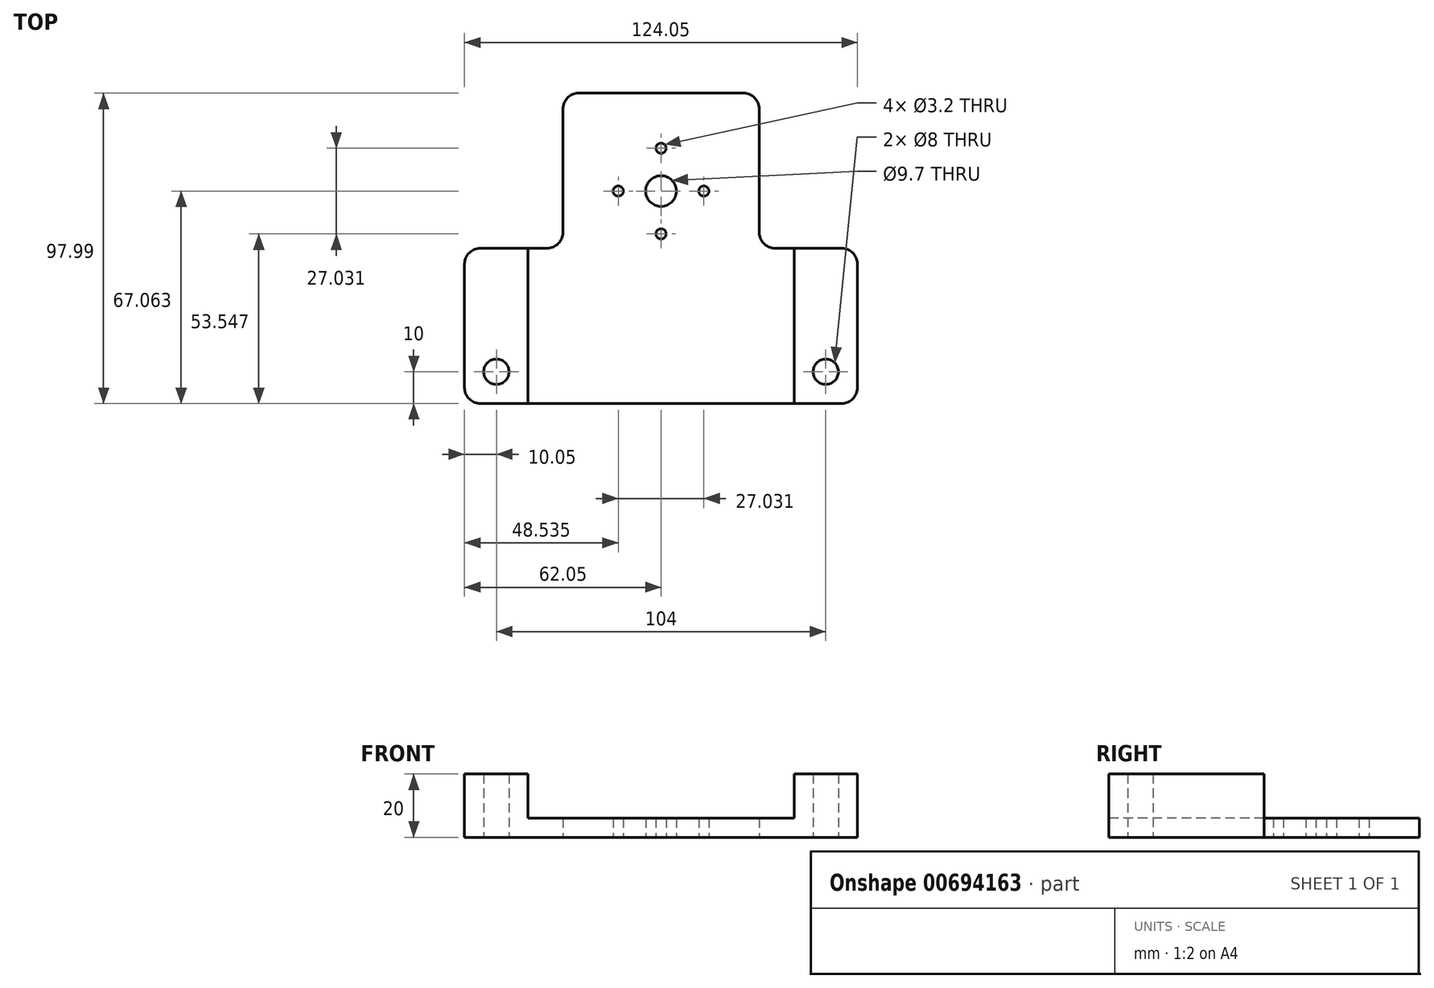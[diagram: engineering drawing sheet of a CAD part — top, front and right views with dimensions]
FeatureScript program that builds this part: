
annotation { "Feature Type Name" : "Feature", "Feature Type Description" : "" }
export const myFeature = defineFeature(function(context is Context, id is Id, definition is map)
    precondition{}
    {
        {
            var Q0;
            Q0=qCreatedBy(makeId("Top.planeOp"),FACE);
            var sketch = newSketch(context, id + "F0", { "sketchPlane" : qUnion([Q0])});
            skLineSegment(sketch, "E0", {"start": v(0, -67) * mm, "end": v(-52, -67) * mm});
            skLineSegment(sketch, "E1", {"start": v(0, -67) * mm, "end": v(52, -67) * mm});
            skCircle(sketch, "E2", {"center": v(52, -67) * mm, "radius": 4 * mm});
            skCircle(sketch, "E3", {"center": v(-52, -67) * mm, "radius": 4 * mm});
            skPoint(sketch, "E4.visualSharp", {"position": v(-62.05, -77) * mm});
            skArc(sketch, "E4.filletArc", {"start": v(-62.05, -72) * mm, "mid": v(-60.58, -75.54) * mm, "end": v(-57.05, -77) * mm});
            skPoint(sketch, "E5.visualSharp", {"position": v(62, -77) * mm});
            skArc(sketch, "E5.filletArc", {"start": v(57, -77) * mm, "mid": v(60.54, -75.54) * mm, "end": v(62, -72) * mm});
            skLineSegment(sketch, "E6", {"start": v(62, -77) * mm, "end": v(62, -33) * mm});
            skLineSegment(sketch, "E7", {"start": v(57, -28) * mm, "end": v(36, -28) * mm});
            skLineSegment(sketch, "E8", {"start": v(31, -23) * mm, "end": v(31, 16) * mm});
            skLineSegment(sketch, "E9", {"start": v(26, 21) * mm, "end": v(-26, 21) * mm});
            skLineSegment(sketch, "E10", {"start": v(-31, 16) * mm, "end": v(-31, -23) * mm});
            skLineSegment(sketch, "E11", {"start": v(-36, -28) * mm, "end": v(-57.05, -28) * mm});
            skPoint(sketch, "E12.visualSharp", {"position": v(-31, 21) * mm});
            skArc(sketch, "E12.filletArc", {"start": v(-26, 21) * mm, "mid": v(-29.54, 19.53) * mm, "end": v(-31, 16) * mm});
            skPoint(sketch, "E13.visualSharp", {"position": v(31, 21) * mm});
            skArc(sketch, "E13.filletArc", {"start": v(31, 16) * mm, "mid": v(29.54, 19.53) * mm, "end": v(26, 21) * mm});
            skPoint(sketch, "E14.visualSharp", {"position": v(31, -28) * mm});
            skArc(sketch, "E14.filletArc", {"start": v(31, -23) * mm, "mid": v(32.46, -26.54) * mm, "end": v(36, -28) * mm});
            skPoint(sketch, "E15.visualSharp", {"position": v(62, -28) * mm});
            skArc(sketch, "E15.filletArc", {"start": v(62, -33) * mm, "mid": v(60.54, -29.46) * mm, "end": v(57, -28) * mm});
            skPoint(sketch, "E16.visualSharp", {"position": v(-62.05, -28) * mm});
            skArc(sketch, "E16.filletArc", {"start": v(-57.05, -28) * mm, "mid": v(-60.58, -29.46) * mm, "end": v(-62.05, -33) * mm});
            skPoint(sketch, "E17.visualSharp", {"position": v(-31, -28) * mm});
            skArc(sketch, "E17.filletArc", {"start": v(-36, -28) * mm, "mid": v(-32.46, -26.54) * mm, "end": v(-31, -23) * mm});
            skLineSegment(sketch, "E18", {"start": v(-62.05, -33) * mm, "end": v(-62.05, -72) * mm});
            skLineSegment(sketch, "E19", {"start": v(-42, -77) * mm, "end": v(-42, -28) * mm});
            skLineSegment(sketch, "E20", {"start": v(-57.05, -77) * mm, "end": v(57, -77) * mm});
            skLineSegment(sketch, "E21", {"start": v(42, -77) * mm, "end": v(42, -28) * mm});
            skCircle(sketch, "E22", {"center": v(0, -9.94) * mm, "radius": 4.85 * mm});
            skCircle(sketch, "E23", {"center": v(13.52, -9.94) * mm, "radius": 1.6 * mm});
            skCircle(sketch, "E24.1.0", {"center": v(0, 3.58) * mm, "radius": 1.6 * mm});
            skCircle(sketch, "E24.2.0", {"center": v(-13.52, -9.94) * mm, "radius": 1.6 * mm});
            skCircle(sketch, "E24.3.0", {"center": v(0, -23.45) * mm, "radius": 1.6 * mm});
            skSolve(sketch);
        }
        {
            var Q0;
            Q0=makeQuery(id+"F0.imprint","IMPRINT",FACE,{"disambiguationData":[TD([[makeQuery(id+"F0.imprint","IMPRINT",EDGE,{"derivedFrom":sQuery(id+"F0.wireOp",EDGE,"E8")}),1.0]])]});
            var Q1;
            {var subQ5=sQuery(id+"F0.wireOp",EDGE,"E0");var subQ7=sQuery(id+"F0.wireOp",EDGE,"E1");var subQ8=makeQuery(id+"F0.imprint","INTERSECT",VERTEX,{"derivedFrom":[subQ5,subQ7]});Q1=makeQuery(id+"F0.imprint","IMPRINT",FACE,{"disambiguationData":[TD([[makeQuery(id+"F0.imprint","IMPRINT",EDGE,{"disambiguationData":[TD([[subQ8,-1.0]])],"derivedFrom":subQ5}),1.0]])]});}
            var Q2;
            Q2=makeQuery(id+"F0.imprint","IMPRINT",FACE,{"disambiguationData":[TD([[makeQuery(id+"F0.imprint","IMPRINT",EDGE,{"derivedFrom":sQuery(id+"F0.wireOp",EDGE,"E3")}),-1.0]])]});
            var Q3;
            Q3=makeQuery(id+"F0.imprint","IMPRINT",FACE,{"disambiguationData":[TD([[makeQuery(id+"F0.imprint","IMPRINT",EDGE,{"derivedFrom":sQuery(id+"F0.wireOp",EDGE,"E2")}),-1.0]])]});
            extrude(context, id + "F1", {"entities" : qUnion([Q0, Q1, Q2, Q3]), "depth" : 6 * mm, "offsetDistance" : 25 * mm});
        }
        {
            var Q0;
            Q0=makeQuery(id+"F0.imprint","IMPRINT",FACE,{"disambiguationData":[TD([[makeQuery(id+"F0.imprint","IMPRINT",EDGE,{"derivedFrom":sQuery(id+"F0.wireOp",EDGE,"E2")}),-1.0]])]});
            var Q1;
            Q1=makeQuery(id+"F0.imprint","IMPRINT",FACE,{"disambiguationData":[TD([[makeQuery(id+"F0.imprint","IMPRINT",EDGE,{"derivedFrom":sQuery(id+"F0.wireOp",EDGE,"E3")}),-1.0]])]});
            extrude(context, id + "F2", {"entities" : qUnion([Q0, Q1]), "operationType" : NewBodyOperationType.ADD, "depth" : 20 * mm, "offsetDistance" : 25 * mm});
        }
    });
